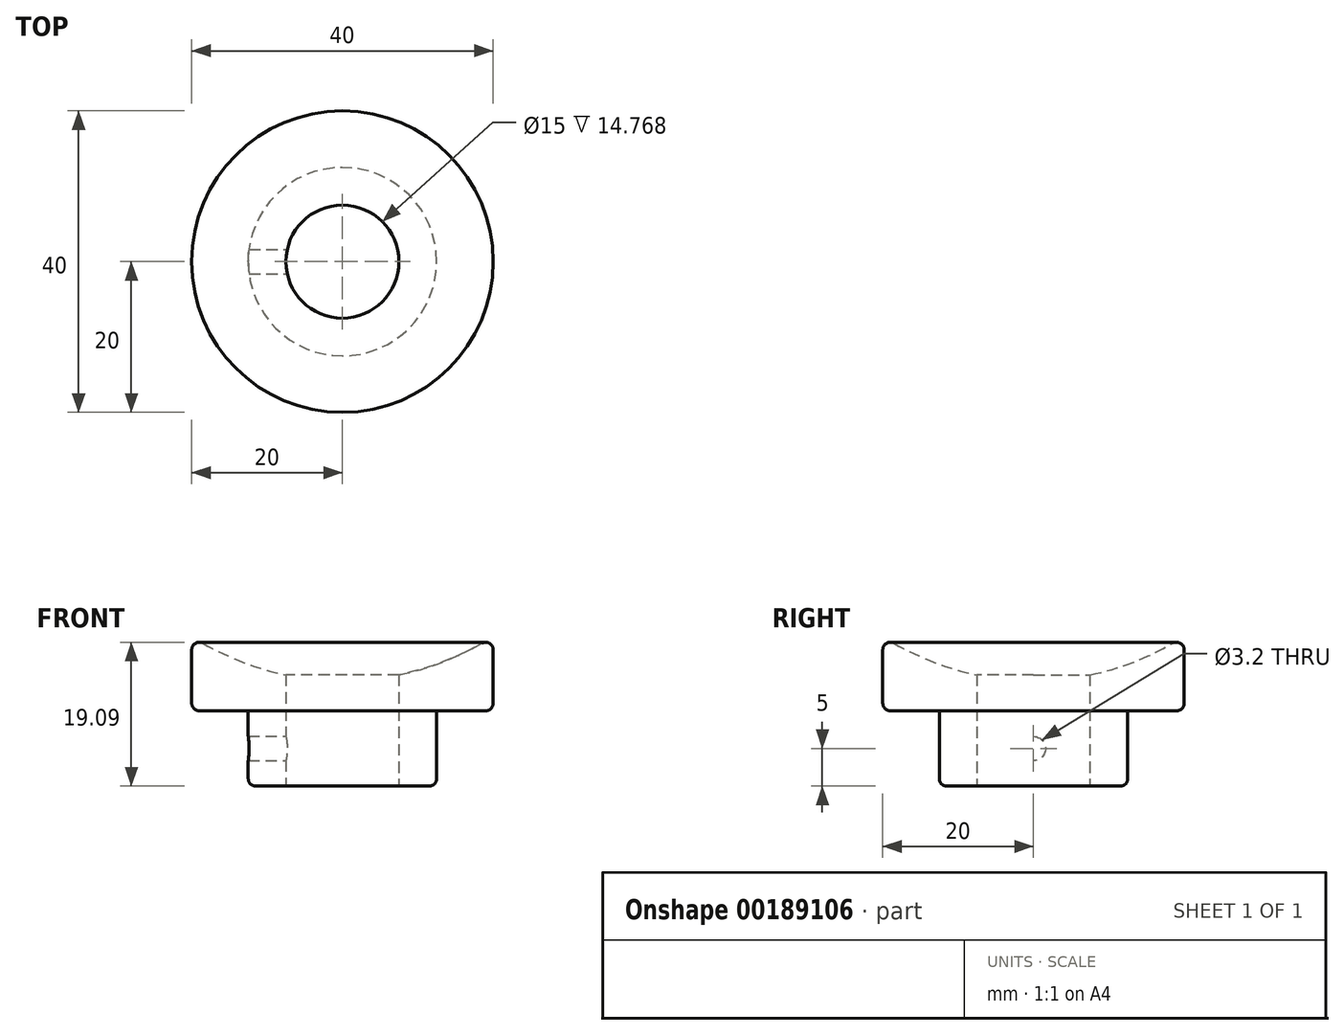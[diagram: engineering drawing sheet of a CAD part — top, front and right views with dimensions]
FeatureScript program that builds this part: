
annotation { "Feature Type Name" : "Feature", "Feature Type Description" : "" }
export const myFeature = defineFeature(function(context is Context, id is Id, definition is map)
    precondition{}
    {
        {
            var Q0;
            Q0=qCreatedBy(makeId("Top.planeOp"),FACE);
            var sketch = newSketch(context, id + "F0", { "sketchPlane" : qUnion([Q0])});
            skCircle(sketch, "E0", {"center": v(0, 0) * mm, "radius": 20 * mm});
            skSolve(sketch);
        }
        {
            var Q0;
            Q0 = qSketchRegion(id + "F0", true);
            extrude(context, id + "F1", {"entities" : qUnion([Q0]), "oppositeDirection" : true, "depth" : 10 * mm});
        }
        {
            var Q0;
            Q0=qCreatedBy(makeId("Front.planeOp"),FACE);
            var sketch = newSketch(context, id + "F2", { "sketchPlane" : qUnion([Q0])});
            skArc(sketch, "E1", {"start": v(0, 68) * mm, "mid": v(-37, 31) * mm, "end": v(0, -6) * mm});
            skLineSegment(sketch, "E2", {"start": v(0, 68) * mm, "end": v(0, -6) * mm});
            skSolve(sketch);
        }
        {
            var Q0;
            Q0 = qSketchRegion(id + "F2", true);
            var Q1;
            Q1=sQuery(id+"F2.wireOp",EDGE,"E2");
            revolve(context, id + "F3", {"operationType" : NewBodyOperationType.REMOVE, "entities" : qUnion([Q0]), "axis" : qUnion([Q1]), "revolveType" : RevolveType.FULL, "oppositeDirection" : true});
        }
        {
            var Q0;
            Q0=makeQuery(id+"F1.opExtrude","CAP_FACE",FACE,{"disambiguationData":[OSD([sQuery(id+"F0.wireOp",EDGE,"E0")])],"isStart":false});
            var sketch = newSketch(context, id + "F4", { "sketchPlane" : qUnion([Q0])});
            skCircle(sketch, "E3", {"center": v(0, 0) * mm, "radius": 12.5 * mm});
            skSolve(sketch);
        }
        {
            var Q0;
            Q0 = qSketchRegion(id + "F4", true);
            extrude(context, id + "F5", {"entities" : qUnion([Q0]), "operationType" : NewBodyOperationType.ADD, "depth" : 10 * mm});
        }
        {
            var Q0;
            Q0=makeQuery(id+"F3.boolean.opBoolean","INTERSECT",EDGE,{"derivedFrom":[makeQuery(id+"F1.opExtrude","SWEPT_FACE",FACE,{"disambiguationData":[OSD([sQuery(id+"F0.wireOp",EDGE,"E0")])]}),makeQuery(id+"F3.opRevolve","SWEPT_FACE",FACE,{"disambiguationData":[OSD([sQuery(id+"F2.wireOp",EDGE,"E1")])]})]});
            var Q1;
            Q1=makeQuery(id+"F1.opExtrude","CAP_EDGE",EDGE,{"disambiguationData":[OSD([sQuery(id+"F0.wireOp",EDGE,"E0")])],"isStart":false});
            var Q2;
            Q2=makeQuery(id+"F5.opExtrude","CAP_EDGE",EDGE,{"disambiguationData":[OSD([sQuery(id+"F4.wireOp",EDGE,"E3")])],"isStart":false});
            fillet(context, id + "F6", {"entities" : qUnion([Q0, Q1, Q2]), "radius" : 1 * mm, "tangentPropagation" : true, "allowEdgeOverflow" : false});
        }
        {
            var Q0;
            Q0=makeQuery(id+"F5.opExtrude","CAP_FACE",FACE,{"disambiguationData":[OSD([sQuery(id+"F4.wireOp",EDGE,"E3")])],"isStart":false});
            var sketch = newSketch(context, id + "F7", { "sketchPlane" : qUnion([Q0])});
            skPoint(sketch, "E4", {"position": v(0, 0) * mm});
            skSolve(sketch);
        }
        {
            var Q0;
            Q0=sQuery(id+"F7.wireOp",VERTEX,"E4");
            var Q1;
            Q1=makeQuery(id+"F1.opExtrude","SWEPT_BODY",BODY,{"disambiguationData":[OSD([sQuery(id+"F0.wireOp",EDGE,"E0")])]});
            hole(context, id + "F8", {"style" : HoleStyle.SIMPLE, "endStyle" : HoleEndStyle.THROUGH, "holeDiameter" : 15 * mm, "locations" : qUnion([Q0]), "scope" : qUnion([Q1]), "isTappedThrough" : true});
        }
        {
            var Q0;
            Q0=qCreatedBy(makeId("Right.planeOp"),FACE);
            var sketch = newSketch(context, id + "F9", { "sketchPlane" : qUnion([Q0])});
            skPoint(sketch, "E5", {"position": v(0, -15) * mm});
            skSolve(sketch);
        }
        {
            var Q0;
            Q0=sQuery(id+"F9.wireOp",VERTEX,"E5");
            var Q1;
            Q1=makeQuery(id+"F1.opExtrude","SWEPT_BODY",BODY,{"disambiguationData":[OSD([sQuery(id+"F0.wireOp",EDGE,"E0")])]});
            hole(context, id + "F10", {"style" : HoleStyle.SIMPLE, "endStyle" : HoleEndStyle.THROUGH, "standardTappedOrClearance" : lookupTablePath({ "standard" : "ISO", "engagement" : "75%", "pitch" : "0.75 mm", "size" : "M4", "type" : "Tapped" }), "standardBlindInLast" : lookupTablePath({ "standard" : "ISO", "engagement" : "75%", "pitch" : "0.75 mm", "size" : "M4", "type" : "Tapped" }), "holeDiameter" : 3.2 * mm, "locations" : qUnion([Q0]), "scope" : qUnion([Q1]), "isTappedThrough" : true, "showTappedDepth" : true});
        }
    });
